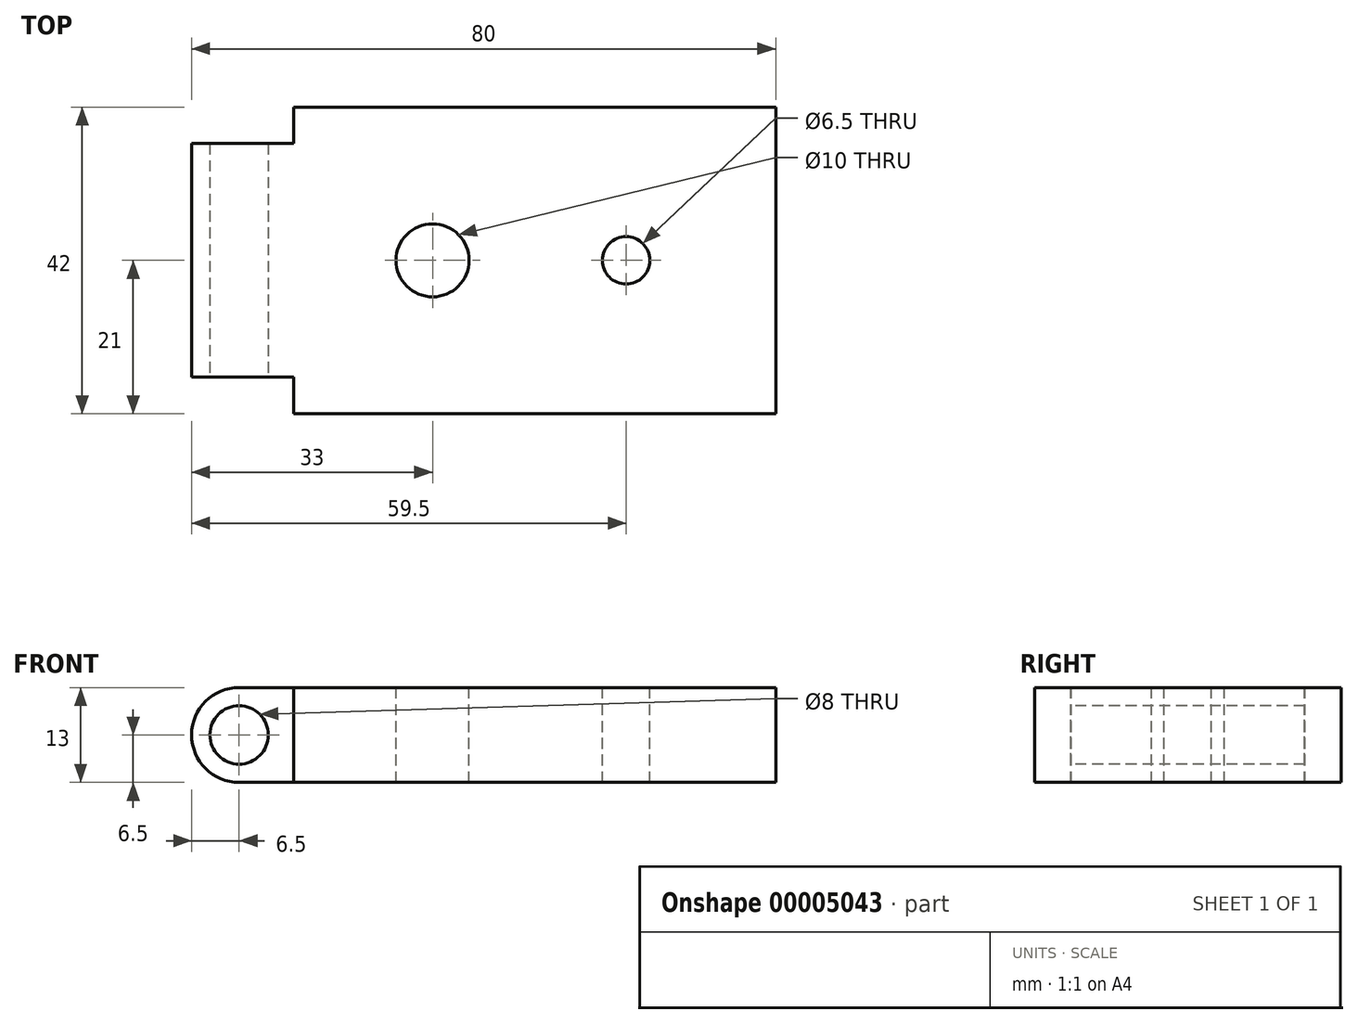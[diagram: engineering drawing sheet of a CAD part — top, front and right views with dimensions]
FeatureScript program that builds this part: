
annotation { "Feature Type Name" : "Feature", "Feature Type Description" : "" }
export const myFeature = defineFeature(function(context is Context, id is Id, definition is map)
    precondition{}
    {
        {
            var Q0;
            Q0=qCreatedBy(makeId("Top.planeOp"),FACE);
            var sketch = newSketch(context, id + "F0", { "sketchPlane" : qUnion([Q0])});
            skLineSegment(sketch, "E0.rect.bottom", {"start": v(40, 21) * mm, "end": v(-40, 21) * mm});
            skLineSegment(sketch, "E0.rect.top", {"start": v(40, -21) * mm, "end": v(-40, -21) * mm});
            skLineSegment(sketch, "E0.rect.left", {"start": v(40, 21) * mm, "end": v(40, -21) * mm});
            skLineSegment(sketch, "E0.rect.right", {"start": v(-40, 21) * mm, "end": v(-40, -21) * mm});
            skPoint(sketch, "E0.rect.middle", {"position": v(0, 0) * mm});
            skSolve(sketch);
        }
        {
            var Q0;
            Q0 = qSketchRegion(id + "F0", true);
            extrude(context, id + "F1", {"entities" : qUnion([Q0]), "depth" : 13 * mm});
        }
        {
            var Q0;
            Q0=makeQuery(id+"F1.opExtrude","CAP_FACE",FACE,{"disambiguationData":[OSD([sQuery(id+"F0.wireOp",EDGE,"E0.rect.bottom"),sQuery(id+"F0.wireOp",EDGE,"E0.rect.top"),sQuery(id+"F0.wireOp",EDGE,"E0.rect.left"),sQuery(id+"F0.wireOp",EDGE,"E0.rect.right")])],"isStart":false});
            var sketch = newSketch(context, id + "F2", { "sketchPlane" : qUnion([Q0])});
            skPoint(sketch, "E1", {"position": v(-40, 16) * mm});
            skPoint(sketch, "E2", {"position": v(-40, -16) * mm});
            skLineSegment(sketch, "E3", {"start": v(-40, 16) * mm, "end": v(-26, 16) * mm});
            skLineSegment(sketch, "E4", {"start": v(-26, 16) * mm, "end": v(-26, 21) * mm});
            skLineSegment(sketch, "E5", {"start": v(-40, -16) * mm, "end": v(-26, -16) * mm});
            skLineSegment(sketch, "E6", {"start": v(-26, -16) * mm, "end": v(-26, -21) * mm});
            skLineSegment(sketch, "E7", {"start": v(-40, 16) * mm, "end": v(-40, 21) * mm});
            skLineSegment(sketch, "E8", {"start": v(-40, 21) * mm, "end": v(-26, 21) * mm});
            skLineSegment(sketch, "E9", {"start": v(-40, -16) * mm, "end": v(-40, -21) * mm});
            skLineSegment(sketch, "E10", {"start": v(-40, -21) * mm, "end": v(-26, -21) * mm});
            skSolve(sketch);
        }
        {
            var Q0;
            Q0 = qSketchRegion(id + "F2", true);
            extrude(context, id + "F3", {"entities" : qUnion([Q0]), "operationType" : NewBodyOperationType.REMOVE, "oppositeDirection" : true, "depth" : 25 * mm});
        }
        {
            var Q0;
            Q0=makeQuery(id+"F3.boolean.opBoolean","COPY",FACE,{"derivedFrom":makeQuery(id+"F3.opExtrude","SWEPT_FACE",FACE,{"disambiguationData":[OSD([sQuery(id+"F2.wireOp",EDGE,"E5")])]})});
            var sketch = newSketch(context, id + "F4", { "sketchPlane" : qUnion([Q0])});
            skLineSegment(sketch, "E11", {"start": v(-27, 13) * mm, "end": v(-27, 0) * mm});
            skCircle(sketch, "E12", {"center": v(-33.5, 6.5) * mm, "radius": 4 * mm});
            skSolve(sketch);
        }
        {
            var Q0;
            Q0 = qSketchRegion(id + "F4", true);
            extrude(context, id + "F5", {"entities" : qUnion([Q0]), "operationType" : NewBodyOperationType.REMOVE, "oppositeDirection" : true, "depth" : 125 * mm});
        }
        {
            var Q0;
            Q0=makeQuery(id+"F1.opExtrude","CAP_FACE",FACE,{"disambiguationData":[OSD([sQuery(id+"F0.wireOp",EDGE,"E0.rect.bottom"),sQuery(id+"F0.wireOp",EDGE,"E0.rect.top"),sQuery(id+"F0.wireOp",EDGE,"E0.rect.left"),sQuery(id+"F0.wireOp",EDGE,"E0.rect.right")])],"isStart":false});
            var sketch = newSketch(context, id + "F6", { "sketchPlane" : qUnion([Q0])});
            skPoint(sketch, "E13", {"position": v(40, 0) * mm});
            skPoint(sketch, "E14", {"position": v(19.5, 0) * mm});
            skCircle(sketch, "E15", {"center": v(19.5, 0) * mm, "radius": 3.25 * mm});
            skSolve(sketch);
        }
        {
            var Q0;
            Q0 = qSketchRegion(id + "F6", true);
            extrude(context, id + "F7", {"entities" : qUnion([Q0]), "operationType" : NewBodyOperationType.REMOVE, "oppositeDirection" : true, "depth" : 25 * mm});
        }
        {
            var Q0;
            Q0=makeQuery(id+"F3.boolean.opBoolean","COPY",FACE,{"derivedFrom":makeQuery(id+"F3.opExtrude","SWEPT_FACE",FACE,{"disambiguationData":[OSD([sQuery(id+"F2.wireOp",EDGE,"E5")])]})});
            var sketch = newSketch(context, id + "F8", { "sketchPlane" : qUnion([Q0])});
            skCircle(sketch, "E16", {"center": v(-33.5, 6.5) * mm, "radius": 6.5 * mm});
            skSolve(sketch);
        }
        {
            var Q0;
            {var subQ0=sQuery(id+"F2.wireOp",EDGE,"E5");var subQ1=makeQuery(id+"F3.boolean.opBoolean","COPY",EDGE,{"derivedFrom":makeQuery(id+"F3.opExtrude","CAP_EDGE",EDGE,{"disambiguationData":[OSD([subQ0])],"isStart":true})});var subQ2=sQuery(id+"F8.wireOp",EDGE,"E16");var subQ3=makeQuery(id+"F8.imprint","INTERSECT",VERTEX,{"derivedFrom":[subQ1,subQ2]});Q0=makeQuery(id+"F8.imprint","IMPRINT",FACE,{"disambiguationData":[TD([[makeQuery(id+"F8.imprint","IMPRINT",EDGE,{"disambiguationData":[TD([[subQ3,-1.0]])],"derivedFrom":subQ2}),-1.0]])]});}
            var Q1;
            {var subQ0=sQuery(id+"F0.wireOp",EDGE,"E0.rect.right");var subQ1=sQuery(id+"F2.wireOp",EDGE,"E5");var subQ3=sQuery(id+"F8.wireOp",EDGE,"E16");var subQ5=makeQuery(id+"F3.boolean.opBoolean","COPY",EDGE,{"derivedFrom":makeQuery(id+"F3.opExtrude","SWEPT_EDGE",EDGE,{"disambiguationData":[OSD([subQ0,subQ1,sQuery(id+"F2.wireOp",EDGE,"E9")])]})});var subQ7=makeQuery(id+"F8.imprint","INTERSECT",VERTEX,{"derivedFrom":[subQ5,subQ3]});Q1=makeQuery(id+"F8.imprint","IMPRINT",FACE,{"disambiguationData":[TD([[makeQuery(id+"F8.imprint","IMPRINT",EDGE,{"disambiguationData":[TD([[subQ7,-1.0]])],"derivedFrom":subQ3}),-1.0]])]});}
            extrude(context, id + "F9", {"entities" : qUnion([Q0, Q1]), "operationType" : NewBodyOperationType.REMOVE, "oppositeDirection" : true, "depth" : 125 * mm});
        }
        {
            var Q0;
            Q0=makeQuery(id+"F1.opExtrude","CAP_FACE",FACE,{"disambiguationData":[OSD([sQuery(id+"F0.wireOp",EDGE,"E0.rect.bottom"),sQuery(id+"F0.wireOp",EDGE,"E0.rect.top"),sQuery(id+"F0.wireOp",EDGE,"E0.rect.left"),sQuery(id+"F0.wireOp",EDGE,"E0.rect.right")])],"isStart":false});
            var sketch = newSketch(context, id + "F10", { "sketchPlane" : qUnion([Q0])});
            skPoint(sketch, "E17", {"position": v(-7, 0) * mm});
            skCircle(sketch, "E18", {"center": v(-7, 0) * mm, "radius": 5 * mm});
            skSolve(sketch);
        }
        {
            var Q0;
            Q0 = qSketchRegion(id + "F10", true);
            extrude(context, id + "F11", {"entities" : qUnion([Q0]), "operationType" : NewBodyOperationType.REMOVE, "oppositeDirection" : true, "depth" : 25 * mm});
        }
    });
